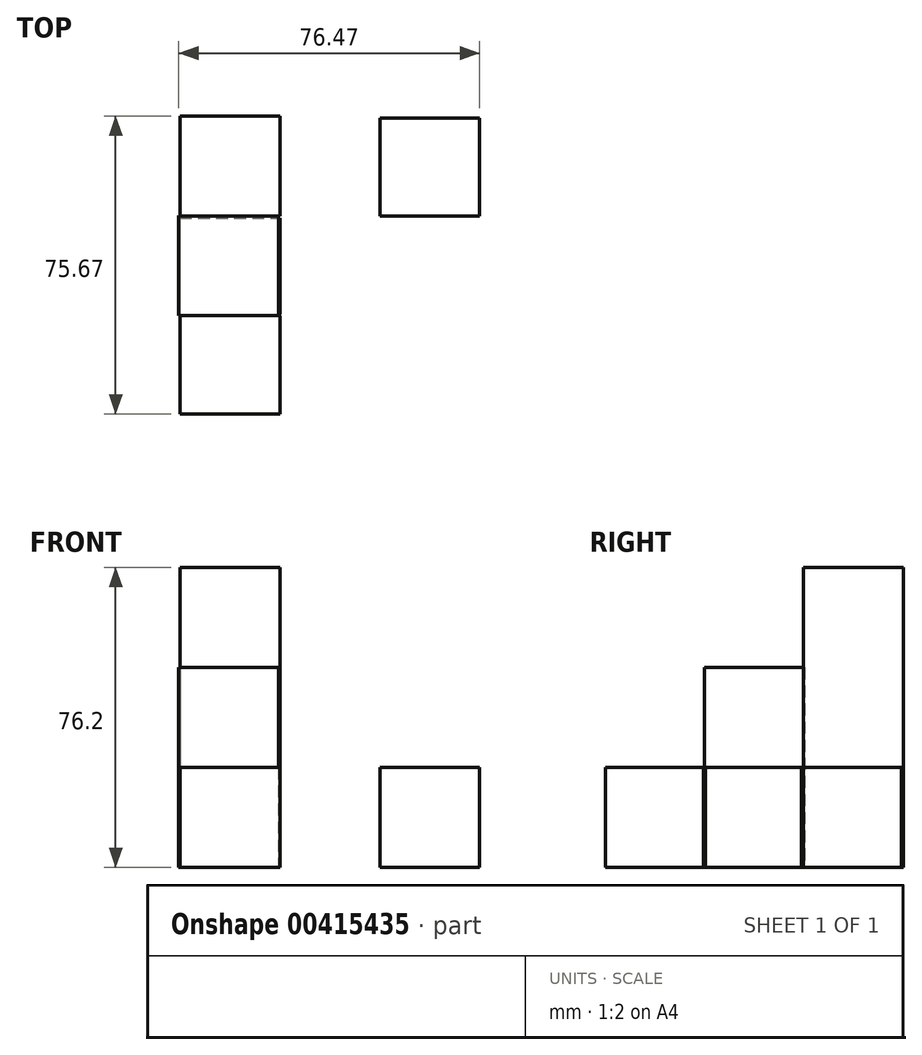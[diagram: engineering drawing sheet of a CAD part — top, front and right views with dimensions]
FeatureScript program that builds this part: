
annotation { "Feature Type Name" : "Feature", "Feature Type Description" : "" }
export const myFeature = defineFeature(function(context is Context, id is Id, definition is map)
    precondition{}
    {
        {
            var Q0;
            Q0=qCreatedBy(makeId("Top.planeOp"),FACE);
            var sketch = newSketch(context, id + "F0", { "sketchPlane" : qUnion([Q0])});
            skLineSegment(sketch, "E0.bottom", {"start": v(38.08, 37.57) * mm, "end": v(-38.08, 37.57) * mm, "construction": true});
            skLineSegment(sketch, "E0.top", {"start": v(38.08, -37.57) * mm, "end": v(-38.08, -37.57) * mm, "construction": true});
            skLineSegment(sketch, "E0.left", {"start": v(38.08, 37.57) * mm, "end": v(38.08, -37.57) * mm, "construction": true});
            skLineSegment(sketch, "E0.right", {"start": v(-38.08, 37.57) * mm, "end": v(-38.08, -37.57) * mm, "construction": true});
            skPoint(sketch, "E0.middle", {"position": v(0, 0) * mm});
            skLineSegment(sketch, "E1.bottom", {"start": v(-38.08, 37.57) * mm, "end": v(-12.17, 37.57) * mm});
            skLineSegment(sketch, "E1.top", {"start": v(-38.08, 12.17) * mm, "end": v(-12.17, 12.17) * mm});
            skLineSegment(sketch, "E1.left", {"start": v(-38.08, 37.57) * mm, "end": v(-38.08, 12.17) * mm});
            skLineSegment(sketch, "E1.right", {"start": v(-12.17, 37.57) * mm, "end": v(-12.17, 12.17) * mm});
            skLineSegment(sketch, "E2.bottom", {"start": v(-38.08, -37.57) * mm, "end": v(-12.68, -37.57) * mm});
            skLineSegment(sketch, "E2.top", {"start": v(-38.08, -12.17) * mm, "end": v(-12.68, -12.17) * mm});
            skLineSegment(sketch, "E2.left", {"start": v(-38.08, -37.57) * mm, "end": v(-38.08, -12.17) * mm});
            skLineSegment(sketch, "E2.right", {"start": v(-12.68, -37.57) * mm, "end": v(-12.68, -12.17) * mm});
            skLineSegment(sketch, "E3.bottom", {"start": v(38.08, 37.57) * mm, "end": v(12.72, 37.57) * mm});
            skLineSegment(sketch, "E3.top", {"start": v(38.08, 12.7) * mm, "end": v(12.72, 12.7) * mm});
            skLineSegment(sketch, "E3.left", {"start": v(38.08, 37.57) * mm, "end": v(38.08, 12.7) * mm});
            skLineSegment(sketch, "E3.right", {"start": v(12.72, 37.57) * mm, "end": v(12.72, 12.7) * mm});
            skLineSegment(sketch, "E4.bottom", {"start": v(-12.17, 37.57) * mm, "end": v(12.72, 37.57) * mm});
            skLineSegment(sketch, "E4.top", {"start": v(-12.17, 12.7) * mm, "end": v(12.72, 12.7) * mm});
            skLineSegment(sketch, "E4.left", {"start": v(-12.17, 37.57) * mm, "end": v(-12.17, 12.7) * mm});
            skLineSegment(sketch, "E5.bottom", {"start": v(-38.08, 12.17) * mm, "end": v(-12.68, 12.17) * mm});
            skLineSegment(sketch, "E5.left", {"start": v(-38.08, 12.17) * mm, "end": v(-38.08, -12.17) * mm});
            skLineSegment(sketch, "E5.right", {"start": v(-12.68, 12.17) * mm, "end": v(-12.68, -12.17) * mm});
            skLineSegment(sketch, "E6.bottom", {"start": v(12.72, 12.7) * mm, "end": v(-12.72, 12.7) * mm});
            skLineSegment(sketch, "E6.top", {"start": v(12.72, -12.7) * mm, "end": v(-12.72, -12.7) * mm});
            skLineSegment(sketch, "E6.left", {"start": v(12.72, 12.7) * mm, "end": v(12.72, -12.7) * mm});
            skLineSegment(sketch, "E6.right", {"start": v(-12.72, 12.7) * mm, "end": v(-12.72, -12.7) * mm});
            skSolve(sketch);
        }
        {
            var Q0;
            Q0=makeQuery(id+"F0.imprint","IMPRINT",FACE,{"disambiguationData":[TD([[makeQuery(id+"F0.imprint","IMPRINT",EDGE,{"derivedFrom":sQuery(id+"F0.wireOp",EDGE,"E3.bottom")}),1.0]])]});
            var Q1;
            Q1=makeQuery(id+"F0.imprint","IMPRINT",FACE,{"disambiguationData":[TD([[makeQuery(id+"F0.imprint","IMPRINT",EDGE,{"derivedFrom":sQuery(id+"F0.wireOp",EDGE,"E2.bottom")}),1.0]])]});
            var Q2;
            Q2=makeQuery(id+"F0.imprint","IMPRINT",FACE,{"disambiguationData":[TD([[makeQuery(id+"F0.imprint","IMPRINT",EDGE,{"derivedFrom":sQuery(id+"F0.wireOp",EDGE,"E1.top")}),-1.0]])]});
            extrude(context, id + "F1", {"entities" : qUnion([Q0, Q1, Q2]), "depth" : 25.4 * mm});
        }
        {
            var Q0;
            Q0=qCreatedBy(makeId("Top.planeOp"),FACE);
            var sketch = newSketch(context, id + "F2", { "sketchPlane" : qUnion([Q0])});
            skLineSegment(sketch, "E7.bottom", {"start": v(38.4, 38.26) * mm, "end": v(-38.4, 38.26) * mm});
            skLineSegment(sketch, "E7.top", {"start": v(38.4, -38.26) * mm, "end": v(-38.4, -38.26) * mm});
            skLineSegment(sketch, "E7.left", {"start": v(38.4, 38.26) * mm, "end": v(38.4, -38.26) * mm});
            skLineSegment(sketch, "E7.right", {"start": v(-38.4, 38.26) * mm, "end": v(-38.4, -38.26) * mm});
            skPoint(sketch, "E7.middle", {"position": v(0, 0) * mm});
            skLineSegment(sketch, "E8.bottom", {"start": v(-38.4, 38.26) * mm, "end": v(12.4, 38.26) * mm, "construction": true});
            skLineSegment(sketch, "E8.top", {"start": v(-38.4, -12.54) * mm, "end": v(12.4, -12.54) * mm, "construction": true});
            skLineSegment(sketch, "E8.left", {"start": v(-38.4, 38.26) * mm, "end": v(-38.4, -12.54) * mm, "construction": true});
            skLineSegment(sketch, "E8.right", {"start": v(12.4, 38.26) * mm, "end": v(12.4, -12.54) * mm, "construction": true});
            skLineSegment(sketch, "E9.bottom", {"start": v(12.4, 38.26) * mm, "end": v(-13, 38.26) * mm});
            skLineSegment(sketch, "E9.top", {"start": v(12.4, 12.86) * mm, "end": v(-13, 12.86) * mm});
            skLineSegment(sketch, "E9.left", {"start": v(12.4, 38.26) * mm, "end": v(12.4, 12.86) * mm});
            skLineSegment(sketch, "E9.right", {"start": v(-13, 38.26) * mm, "end": v(-13, 12.86) * mm});
            skLineSegment(sketch, "E10.bottom", {"start": v(-38.4, -12.54) * mm, "end": v(-13, -12.54) * mm});
            skLineSegment(sketch, "E10.top", {"start": v(-38.4, 12.86) * mm, "end": v(-13, 12.86) * mm});
            skLineSegment(sketch, "E10.left", {"start": v(-38.4, -12.54) * mm, "end": v(-38.4, 12.86) * mm});
            skLineSegment(sketch, "E10.right", {"start": v(-13, -12.54) * mm, "end": v(-13, 12.86) * mm});
            skSolve(sketch);
        }
        {
            var Q0;
            Q0=makeQuery(id+"F2.imprint","IMPRINT",FACE,{"disambiguationData":[TD([[makeQuery(id+"F2.imprint","IMPRINT",EDGE,{"derivedFrom":sQuery(id+"F2.wireOp",EDGE,"E10.bottom")}),1.0]])]});
            var Q1;
            Q1=makeQuery(id+"F2.imprint","IMPRINT",FACE,{"disambiguationData":[TD([[makeQuery(id+"F2.imprint","IMPRINT",EDGE,{"derivedFrom":sQuery(id+"F2.wireOp",EDGE,"E9.bottom")}),1.0]])]});
            extrude(context, id + "F3", {"entities" : qUnion([Q0, Q1]), "depth" : 50.8 * mm});
        }
        {
            var Q0;
            Q0=qCreatedBy(makeId("Top.planeOp"),FACE);
            var sketch = newSketch(context, id + "F4", { "sketchPlane" : qUnion([Q0])});
            skLineSegment(sketch, "E11.bottom", {"start": v(38.1, 38.1) * mm, "end": v(-38.1, 38.1) * mm, "construction": true});
            skLineSegment(sketch, "E11.top", {"start": v(38.1, -38.1) * mm, "end": v(-38.1, -38.1) * mm, "construction": true});
            skLineSegment(sketch, "E11.left", {"start": v(38.1, 38.1) * mm, "end": v(38.1, -38.1) * mm, "construction": true});
            skLineSegment(sketch, "E11.right", {"start": v(-38.1, 38.1) * mm, "end": v(-38.1, -38.1) * mm, "construction": true});
            skPoint(sketch, "E11.middle", {"position": v(0, 0) * mm});
            skLineSegment(sketch, "E12.bottom", {"start": v(-38.1, 38.1) * mm, "end": v(-12.7, 38.1) * mm});
            skLineSegment(sketch, "E12.top", {"start": v(-38.1, 12.7) * mm, "end": v(-12.7, 12.7) * mm});
            skLineSegment(sketch, "E12.left", {"start": v(-38.1, 38.1) * mm, "end": v(-38.1, 12.7) * mm});
            skLineSegment(sketch, "E12.right", {"start": v(-12.7, 38.1) * mm, "end": v(-12.7, 12.7) * mm});
            skSolve(sketch);
        }
        {
            var Q0;
            Q0 = qSketchRegion(id + "F4", true);
            extrude(context, id + "F5", {"entities" : qUnion([Q0]), "depth" : 76.2 * mm});
        }
    });
